# Revit family: WIR
name_source: partatom
category: Plumbing Fixtures
revit_build: Autodesk Revit 2015 (Build: 20140322_1515(x64)
units: mm (PartAtom-declared; Revit-internal decimal feet)

## types (3) — shared parameters
Conglomerate = <By Category>
Glass = Glass
Manufacturer = SanSwiss
Metal = Aluminum - Polished
Model = WIR
Outlet pipe nominal diameter = 50 mm
Type Comments = ILA
URL = www.sanswiss.com
Water flow rate = 0.6 L/s
x = 74 mm
zero-valued in all types: Number of elements

## per-type parameters (varying)
| type | A | B | Shower base | y |
| 900x900 | 900 mm  [stored 2.95276 ft] | 900 mm  [stored 2.95276 ft] | shower base_arc_ : 900x900 | 605 mm |
| 800x800 | 800 mm  [stored 2.62467 ft] | 800 mm  [stored 2.62467 ft] | shower base_arc_ : 800x800 | 505 mm |
| 1000x1000 | 1000 mm  [stored 3.28084 ft] | 1000 mm  [stored 3.28084 ft] | shower base_arc_ : 1000x1000 | 705 mm |

note: [stored X ft] marks values corroborated as IEEE doubles in the binary element streams (Revit-internal decimal feet)

## geometry (parser evidence)
native form markers: Sweep x27
no freeform markers — native parametric forms only
